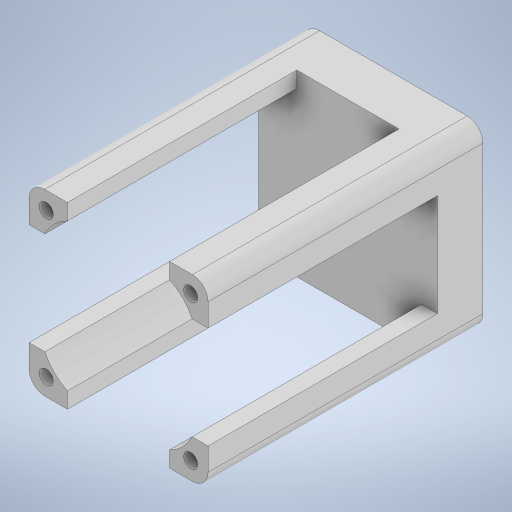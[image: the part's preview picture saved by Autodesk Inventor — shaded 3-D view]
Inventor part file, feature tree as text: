
AUTODESK INVENTOR PART (.ipt)
format: ipt  version: 2024 (Build 280153000, 153)  size: 287,232 bytes
history: native  units: in
note: dims shown in document units (in); Inventor stores cm internally (conversion verified against a paired STEP export)
features: extrude x3, sketch x3, fillet x2
ambient origin geometry x8: Origin, YZ Plane, XZ Plane, XY Plane, X Axis, Y Axis, Z Axis, Center Point
bodies: Solid1 (feature_tree)
feature tree (8):
  extrude  "Extrusion1"  Depth=4.4882in
  fillet  "Fillet1"  Radius=6.8898in
  fillet  "Fillet2"  Radius=0.3937in
  extrude  "Extrusion3"  Depth=0.3937in
  extrude  "Extrusion5"  Depth=5.748in
  sketch  "Sketch1"  dims[d0=4.4882in d1=4.4882in d2=6.8898in d3=0.0in d9=0.3937in]
  sketch  "Sketch3"  dims[d10=0.3937in d11=0.3543in]
  sketch  "Sketch6"  dims[d12=0.4346in d13=0.4346in d14=0.3543in d15=0.3543in d16=0.3543in d17=0.4346in d18=0.4346in d19=0.4346in d20=0.4346in d21=0.4346in d22=0.4346in d23=5.748in d24=0.0in d30=0.5709in d31=0.3988in d32=0.5709in d33=0.3988in d34=1.1811in d35=0.5709in d36=0.3988in d37=0.5709in d38=0.3988in d39=1.1811in d40=0.5709in d41=0.3988in d42=0.5709in d44=1.1811in d45=0.3988in d46=0.5709in d47=0.3988in d48=0.5709in d49=0.3988in d50=1.1811in d51=5.748in d52=2.874in d53=0.0in d54=0.0in d28=0.0197in d29=0.0344in]
